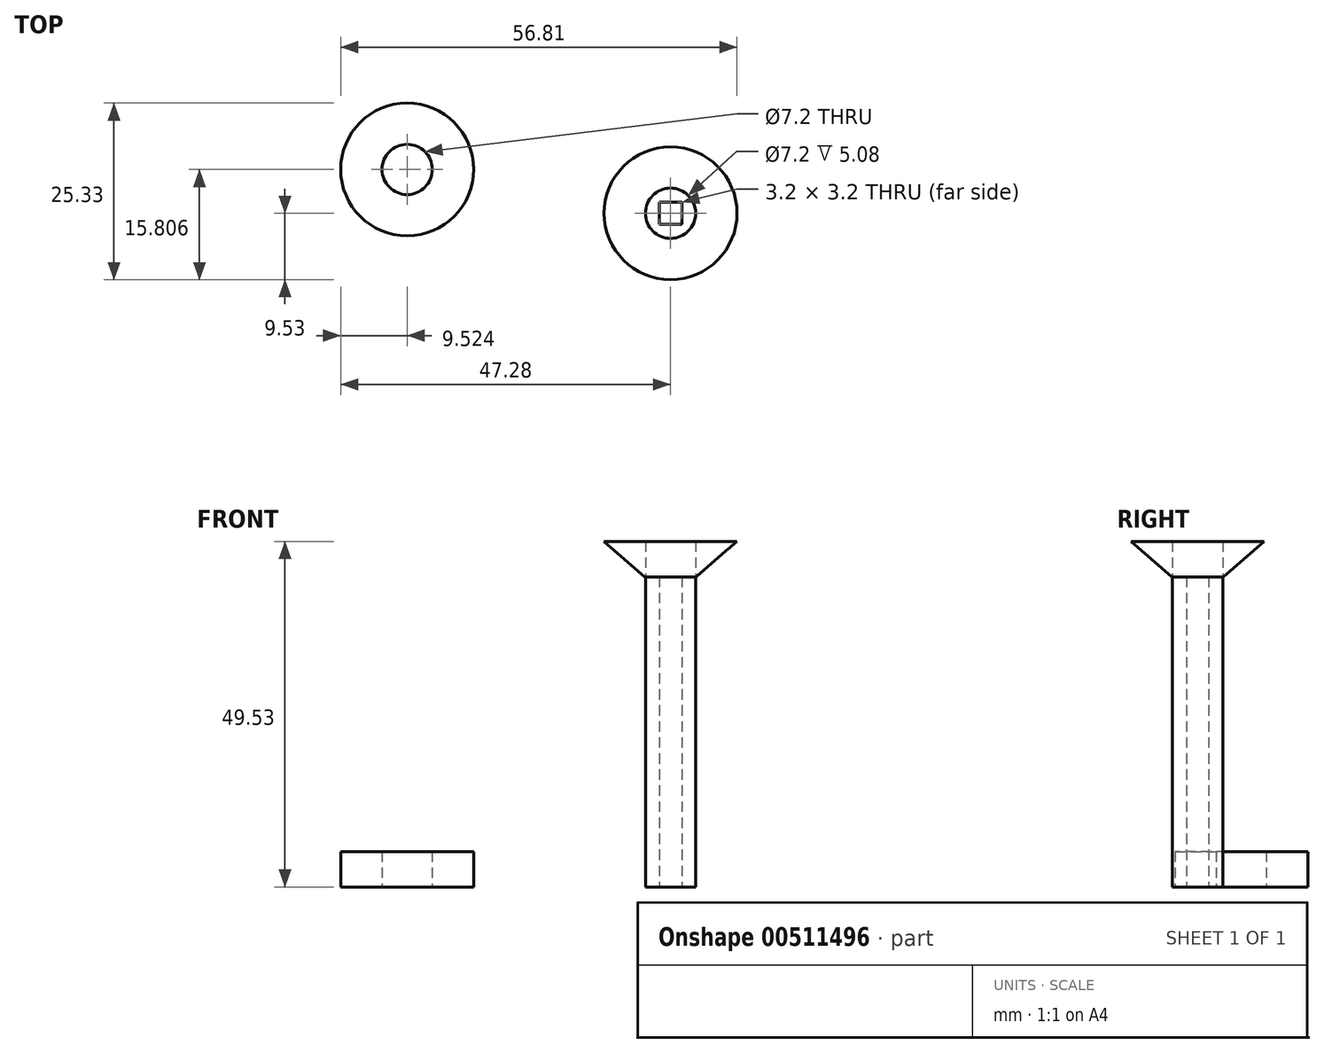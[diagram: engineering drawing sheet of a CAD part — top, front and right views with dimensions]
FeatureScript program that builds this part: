
annotation { "Feature Type Name" : "Feature", "Feature Type Description" : "" }
export const myFeature = defineFeature(function(context is Context, id is Id, definition is map)
    precondition{}
    {
        {
            var Q0;
            Q0=qCreatedBy(makeId("Top.planeOp"),FACE);
            var sketch = newSketch(context, id + "F0", { "sketchPlane" : qUnion([Q0])});
            skCircle(sketch, "E0", {"center": v(0, 0) * mm, "radius": 3.6 * mm});
            skSolve(sketch);
        }
        {
            var Q0;
            Q0=makeQuery(id+"F0.imprint","IMPRINT",FACE,{"disambiguationData":[TD([[makeQuery(id+"F0.imprint","IMPRINT",EDGE,{"derivedFrom":sQuery(id+"F0.wireOp",EDGE,"E0")}),1.0]])]});
            extrude(context, id + "F1", {"entities" : qUnion([Q0]), "depth" : 44.45 * mm});
        }
        {
            var Q0;
            Q0=makeQuery(id+"F1.opExtrude","CAP_FACE",FACE,{"disambiguationData":[OSD([sQuery(id+"F0.wireOp",EDGE,"E0")])],"isStart":true});
            var sketch = newSketch(context, id + "F2", { "sketchPlane" : qUnion([Q0])});
            skLineSegment(sketch, "E1.bottom", {"start": v(1.6, -1.6) * mm, "end": v(-1.6, -1.6) * mm});
            skLineSegment(sketch, "E1.top", {"start": v(1.6, 1.6) * mm, "end": v(-1.6, 1.6) * mm});
            skLineSegment(sketch, "E1.left", {"start": v(1.6, -1.6) * mm, "end": v(1.6, 1.6) * mm});
            skLineSegment(sketch, "E1.right", {"start": v(-1.6, -1.6) * mm, "end": v(-1.6, 1.6) * mm});
            skPoint(sketch, "E1.middle", {"position": v(0, 0) * mm});
            skSolve(sketch);
        }
        {
            var Q0;
            Q0=makeQuery(id+"F2.imprint","IMPRINT",FACE,{"disambiguationData":[TD([[makeQuery(id+"F2.imprint","IMPRINT",EDGE,{"derivedFrom":sQuery(id+"F2.wireOp",EDGE,"E1.bottom")}),-1.0]])]});
            extrude(context, id + "F3", {"entities" : qUnion([Q0]), "operationType" : NewBodyOperationType.REMOVE, "oppositeDirection" : true, "depth" : 45.47 * mm});
        }
        {
            var Q0;
            Q0=makeQuery(id+"F1.opExtrude","CAP_FACE",FACE,{"disambiguationData":[OSD([sQuery(id+"F0.wireOp",EDGE,"E0")])],"isStart":false});
            var sketch = newSketch(context, id + "F4", { "sketchPlane" : qUnion([Q0])});
            skCircle(sketch, "E2", {"center": v(0, 0) * mm, "radius": 9.53 * mm});
            skSolve(sketch);
        }
        {
            var Q0;
            Q0=makeQuery(id+"F4.imprint","IMPRINT",FACE,{"disambiguationData":[TD([[makeQuery(id+"F4.imprint","IMPRINT",EDGE,{"derivedFrom":sQuery(id+"F4.wireOp",EDGE,"E2")}),1.0]])]});
            extrude(context, id + "F5", {"entities" : qUnion([Q0]), "depth" : 5.08 * mm});
        }
        {
            var Q0;
            Q0=makeQuery(id+"F5.opExtrude","CAP_EDGE",EDGE,{"disambiguationData":[OSD([sQuery(id+"F4.wireOp",EDGE,"E2")])],"isStart":true});
            chamfer(context, id + "F6", {"entities" : qUnion([Q0]), "chamferType" : ChamferType.TWO_OFFSETS, "width1" : 5.08 * mm, "oppositeDirection" : false, "width2" : 5.84 * mm, "tangentPropagation" : true});
        }
        {
            var Q0;
            Q0=qCreatedBy(makeId("Top.planeOp"),FACE);
            var sketch = newSketch(context, id + "F7", { "sketchPlane" : qUnion([Q0])});
            skCircle(sketch, "E3", {"center": v(-37.76, 6.28) * mm, "radius": 9.53 * mm});
            skSolve(sketch);
        }
        {
            var Q0;
            Q0=makeQuery(id+"F7.imprint","IMPRINT",FACE,{"disambiguationData":[TD([[makeQuery(id+"F7.imprint","IMPRINT",EDGE,{"derivedFrom":sQuery(id+"F7.wireOp",EDGE,"E3")}),1.0]])]});
            extrude(context, id + "F8", {"entities" : qUnion([Q0]), "depth" : 5.08 * mm});
        }
        {
            var Q0;
            Q0=makeQuery(id+"F8.opExtrude","CAP_FACE",FACE,{"disambiguationData":[OSD([sQuery(id+"F7.wireOp",EDGE,"E3")])],"isStart":true});
            var sketch = newSketch(context, id + "F9", { "sketchPlane" : qUnion([Q0])});
            skCircle(sketch, "E4", {"center": v(-37.76, -6.28) * mm, "radius": 3.6 * mm});
            skSolve(sketch);
        }
        {
            var Q0;
            Q0=makeQuery(id+"F9.imprint","IMPRINT",FACE,{"disambiguationData":[TD([[makeQuery(id+"F9.imprint","IMPRINT",EDGE,{"derivedFrom":sQuery(id+"F9.wireOp",EDGE,"E4")}),1.0]])]});
            extrude(context, id + "F10", {"entities" : qUnion([Q0]), "operationType" : NewBodyOperationType.REMOVE, "oppositeDirection" : true, "depth" : 6.1 * mm});
        }
    });
